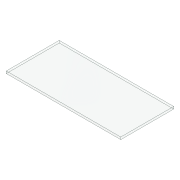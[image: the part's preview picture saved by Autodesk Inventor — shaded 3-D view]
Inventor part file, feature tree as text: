
AUTODESK INVENTOR PART (.ipt)
format: ipt  version: 2020.3 (Build 243373010, 373A)  size: 76,800 bytes
history: native  units: mm
features: other x3, sketch x1
ambient origin geometry x8: Origin, YZ Plane, XZ Plane, XY Plane, X Axis, Y Axis, Z Axis, Center Point
bodies: Solid1 (feature_tree)
feature tree (4):
  other  "GlassSaver.ipt"
  other  "Solid1::GlassSaver.ipt"
  other  "TaggingFeature1"
  sketch  "Sketch1"  dims[d0=10.0mm]
